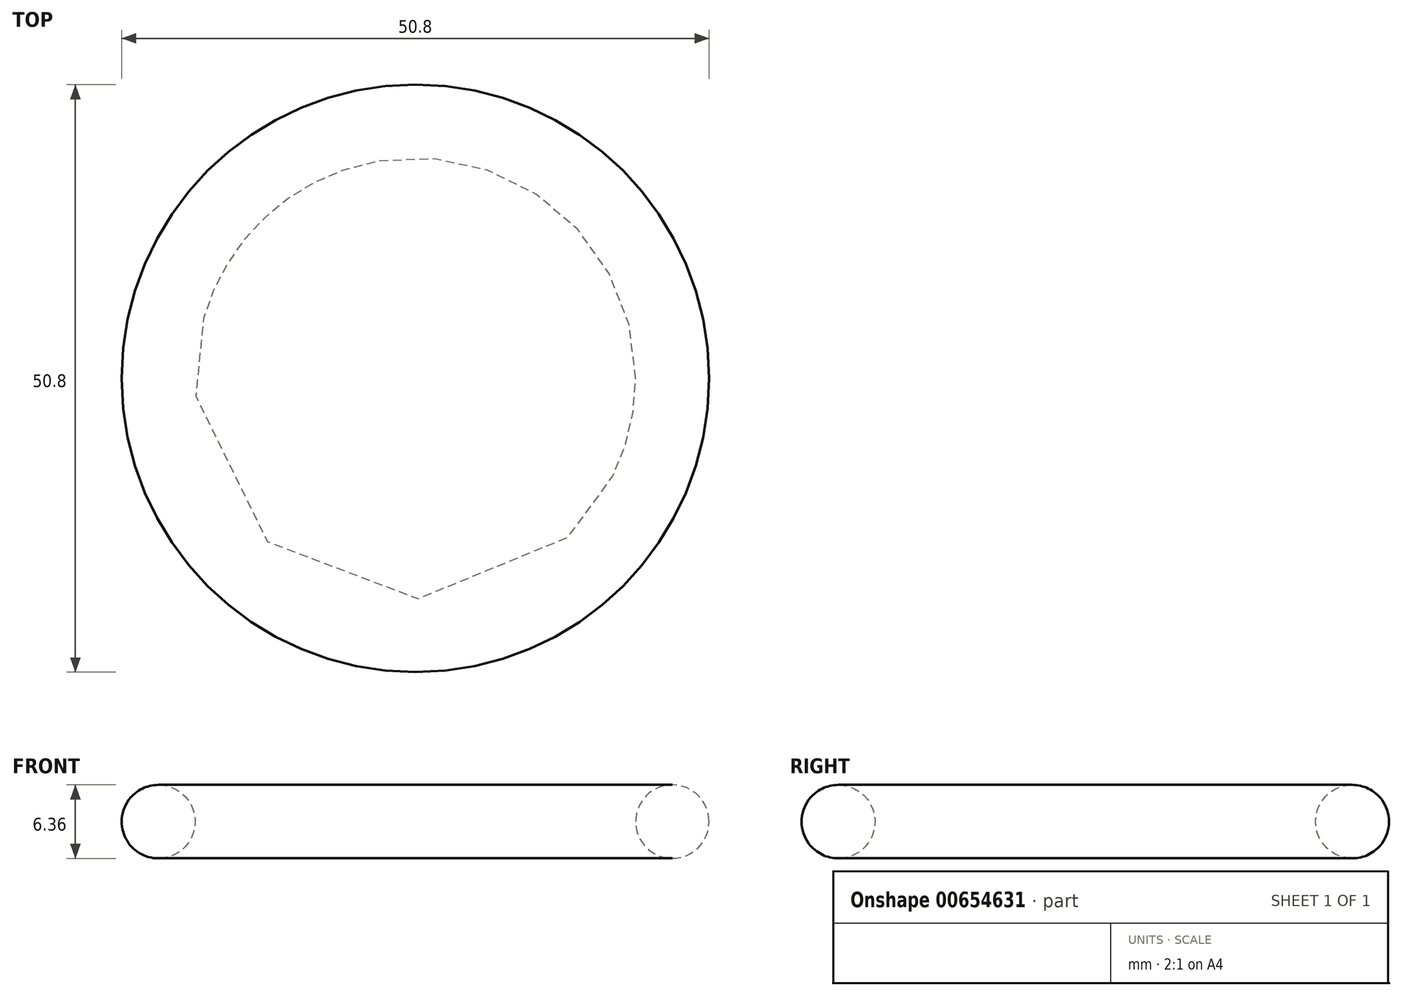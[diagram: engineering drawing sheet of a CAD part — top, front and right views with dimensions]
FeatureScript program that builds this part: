
annotation { "Feature Type Name" : "Feature", "Feature Type Description" : "" }
export const myFeature = defineFeature(function(context is Context, id is Id, definition is map)
    precondition{}
    {
        {
            var Q0;
            Q0=qCreatedBy(makeId("Front.planeOp"),FACE);
            var sketch = newSketch(context, id + "F0", { "sketchPlane" : qUnion([Q0])});
            skCircle(sketch, "E0", {"center": v(-22.23, 0) * mm, "radius": 3.17 * mm});
            skLineSegment(sketch, "E1", {"start": v(0, 12) * mm, "end": v(0, -11.05) * mm, "construction": true});
            skSolve(sketch);
        }
        {
            var Q0;
            Q0 = qSketchRegion(id + "F0", true);
            var Q1;
            Q1=sQuery(id+"F0.wireOp",EDGE,"E1");
            revolve(context, id + "F1", {"entities" : qUnion([Q0]), "axis" : qUnion([Q1]), "revolveType" : RevolveType.FULL});
        }
    });
